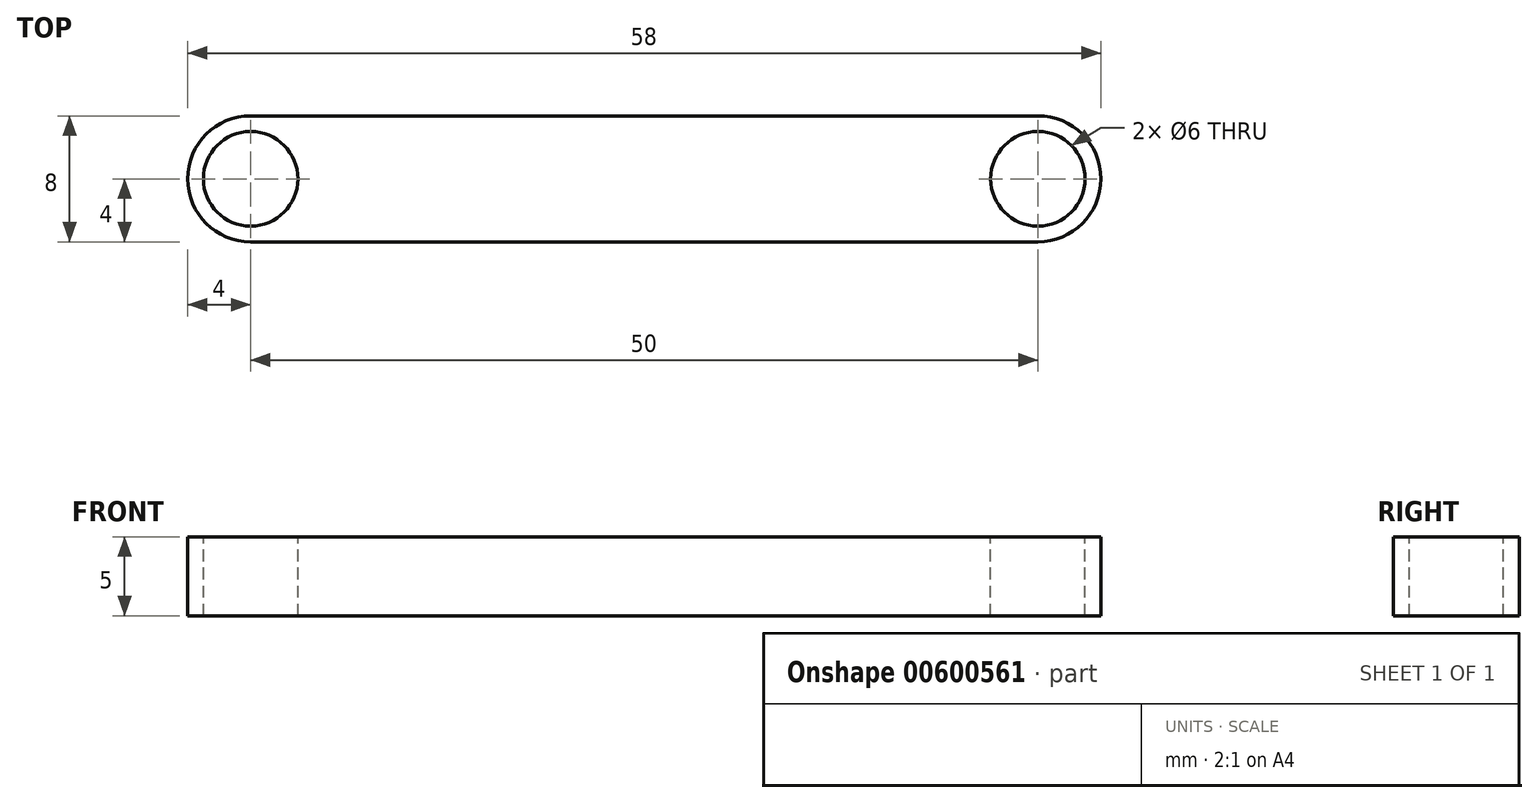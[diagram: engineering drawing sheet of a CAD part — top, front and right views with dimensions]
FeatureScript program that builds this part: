
annotation { "Feature Type Name" : "Feature", "Feature Type Description" : "" }
export const myFeature = defineFeature(function(context is Context, id is Id, definition is map)
    precondition{}
    {
        {
            var Q0;
            Q0=qCreatedBy(makeId("Top.planeOp"),FACE);
            var sketch = newSketch(context, id + "F0", { "sketchPlane" : qUnion([Q0])});
            skLineSegment(sketch, "E0", {"start": v(0, 0) * mm, "end": v(50, 0) * mm, "construction": true});
            skArc(sketch, "E1.0.startCap", {"start": v(0, -4) * mm, "mid": v(-4, 0) * mm, "end": v(0, 4) * mm});
            skArc(sketch, "E1.0.endCap", {"start": v(50, 4) * mm, "mid": v(54, 0) * mm, "end": v(50, -4) * mm});
            skLineSegment(sketch, "E1.0.left", {"start": v(0, 4) * mm, "end": v(50, 4) * mm});
            skLineSegment(sketch, "E1.0.right", {"start": v(0, -4) * mm, "end": v(50, -4) * mm});
            skSolve(sketch);
        }
        {
            var Q0;
            Q0 = qSketchRegion(id + "F0", true);
            extrude(context, id + "F1", {"entities" : qUnion([Q0]), "depth" : 5 * mm, "offsetDistance" : 25 * mm});
        }
        {
            var Q0;
            Q0=makeQuery(id+"F1.opExtrude","CAP_FACE",FACE,{"disambiguationData":[OSD([sQuery(id+"F0.wireOp",EDGE,"E1.0.startCap"),sQuery(id+"F0.wireOp",EDGE,"E1.0.endCap"),sQuery(id+"F0.wireOp",EDGE,"E1.0.left"),sQuery(id+"F0.wireOp",EDGE,"E1.0.right")])],"isStart":false});
            var sketch = newSketch(context, id + "F2", { "sketchPlane" : qUnion([Q0])});
            skCircle(sketch, "E2", {"center": v(0, 0) * mm, "radius": 3 * mm});
            skSolve(sketch);
        }
        {
            var Q0;
            Q0 = qSketchRegion(id + "F2", true);
            extrude(context, id + "F3", {"entities" : qUnion([Q0]), "operationType" : NewBodyOperationType.REMOVE, "endBound" : BoundingType.UP_TO_NEXT, "oppositeDirection" : true, "depth" : 25 * mm, "offsetDistance" : 25 * mm});
        }
        {
            var Q0;
            Q0=makeQuery(id+"F1.opExtrude","CAP_FACE",FACE,{"disambiguationData":[OSD([sQuery(id+"F0.wireOp",EDGE,"E1.0.startCap"),sQuery(id+"F0.wireOp",EDGE,"E1.0.endCap"),sQuery(id+"F0.wireOp",EDGE,"E1.0.left"),sQuery(id+"F0.wireOp",EDGE,"E1.0.right")])],"isStart":false});
            var sketch = newSketch(context, id + "F4", { "sketchPlane" : qUnion([Q0])});
            skCircle(sketch, "E3", {"center": v(50, 0) * mm, "radius": 3 * mm});
            skSolve(sketch);
        }
        {
            var Q0;
            Q0 = qSketchRegion(id + "F4", true);
            extrude(context, id + "F5", {"entities" : qUnion([Q0]), "operationType" : NewBodyOperationType.REMOVE, "endBound" : BoundingType.UP_TO_NEXT, "oppositeDirection" : true, "depth" : 25 * mm, "offsetDistance" : 25 * mm});
        }
    });
